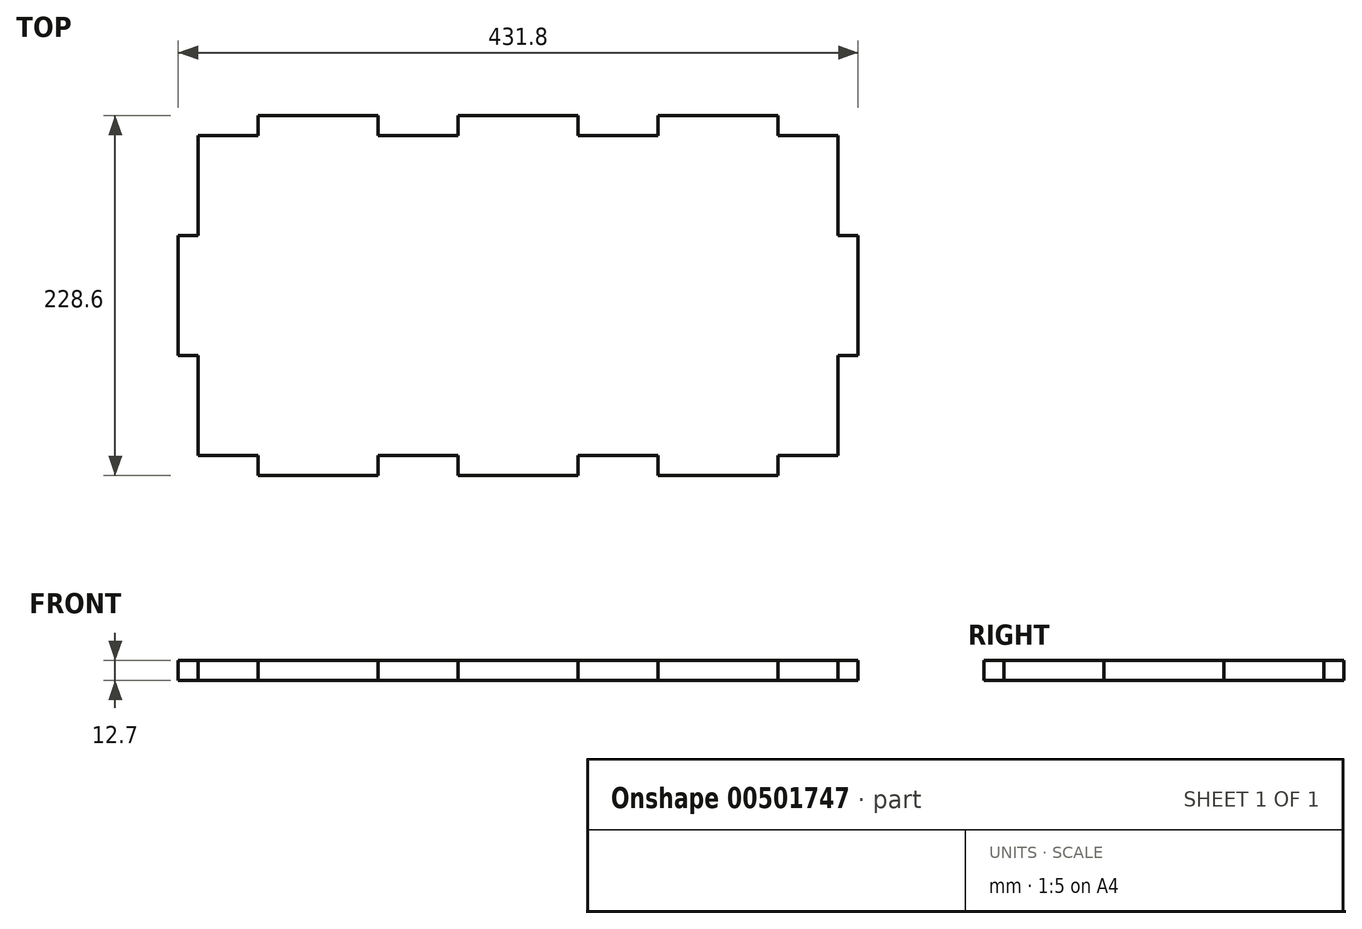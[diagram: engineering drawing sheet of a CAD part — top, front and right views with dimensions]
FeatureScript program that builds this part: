
annotation { "Feature Type Name" : "Feature", "Feature Type Description" : "" }
export const myFeature = defineFeature(function(context is Context, id is Id, definition is map)
    precondition{}
    {
        {
            var Q0;
            Q0=qCreatedBy(makeId("Top.planeOp"),FACE);
            var sketch = newSketch(context, id + "F0", { "sketchPlane" : qUnion([Q0])});
            skLineSegment(sketch, "E0.bottom", {"start": v(-203.2, 101.6) * mm, "end": v(203.2, 101.6) * mm});
            skLineSegment(sketch, "E0.top", {"start": v(-203.2, -101.6) * mm, "end": v(203.2, -101.6) * mm});
            skLineSegment(sketch, "E0.left", {"start": v(-203.2, 101.6) * mm, "end": v(-203.2, -101.6) * mm});
            skLineSegment(sketch, "E0.right", {"start": v(203.2, 101.6) * mm, "end": v(203.2, -101.6) * mm});
            skPoint(sketch, "E0.middle", {"position": v(0, 0) * mm});
            skLineSegment(sketch, "E1.bottom", {"start": v(-38.1, 114.3) * mm, "end": v(38.1, 114.3) * mm});
            skLineSegment(sketch, "E1.top", {"start": v(-38.1, 88.9) * mm, "end": v(38.1, 88.9) * mm});
            skLineSegment(sketch, "E1.left", {"start": v(-38.1, 114.3) * mm, "end": v(-38.1, 88.9) * mm});
            skLineSegment(sketch, "E1.right", {"start": v(38.1, 114.3) * mm, "end": v(38.1, 88.9) * mm});
            skPoint(sketch, "E1.middle", {"position": v(0, 101.6) * mm});
            skLineSegment(sketch, "E2.bottom", {"start": v(-215.9, 38.1) * mm, "end": v(-190.5, 38.1) * mm});
            skLineSegment(sketch, "E2.top", {"start": v(-215.9, -38.1) * mm, "end": v(-190.5, -38.1) * mm});
            skLineSegment(sketch, "E2.left", {"start": v(-215.9, 38.1) * mm, "end": v(-215.9, -38.1) * mm});
            skLineSegment(sketch, "E2.right", {"start": v(-190.5, 38.1) * mm, "end": v(-190.5, -38.1) * mm});
            skPoint(sketch, "E2.middle", {"position": v(-203.2, 0) * mm});
            skLineSegment(sketch, "E3.bottom", {"start": v(-38.1, -88.9) * mm, "end": v(38.1, -88.9) * mm});
            skLineSegment(sketch, "E3.top", {"start": v(-38.1, -114.3) * mm, "end": v(38.1, -114.3) * mm});
            skLineSegment(sketch, "E3.left", {"start": v(-38.1, -88.9) * mm, "end": v(-38.1, -114.3) * mm});
            skLineSegment(sketch, "E3.right", {"start": v(38.1, -88.9) * mm, "end": v(38.1, -114.3) * mm});
            skPoint(sketch, "E3.middle", {"position": v(0, -101.6) * mm});
            skLineSegment(sketch, "E4.bottom", {"start": v(190.5, 38.1) * mm, "end": v(215.9, 38.1) * mm});
            skLineSegment(sketch, "E4.top", {"start": v(190.5, -38.1) * mm, "end": v(215.9, -38.1) * mm});
            skLineSegment(sketch, "E4.left", {"start": v(190.5, 38.1) * mm, "end": v(190.5, -38.1) * mm});
            skLineSegment(sketch, "E4.right", {"start": v(215.9, 38.1) * mm, "end": v(215.9, -38.1) * mm});
            skPoint(sketch, "E4.middle", {"position": v(203.2, 0) * mm});
            skLineSegment(sketch, "E5.bottom", {"start": v(-165.1, -88.9) * mm, "end": v(-88.9, -88.9) * mm});
            skLineSegment(sketch, "E5.top", {"start": v(-165.1, -114.3) * mm, "end": v(-88.9, -114.3) * mm});
            skLineSegment(sketch, "E5.left", {"start": v(-165.1, -88.9) * mm, "end": v(-165.1, -114.3) * mm});
            skLineSegment(sketch, "E5.right", {"start": v(-88.9, -88.9) * mm, "end": v(-88.9, -114.3) * mm});
            skPoint(sketch, "E5.middle", {"position": v(-127, -101.6) * mm});
            skLineSegment(sketch, "E6.bottom", {"start": v(88.9, -88.9) * mm, "end": v(165.1, -88.9) * mm});
            skLineSegment(sketch, "E6.top", {"start": v(88.9, -114.3) * mm, "end": v(165.1, -114.3) * mm});
            skLineSegment(sketch, "E6.left", {"start": v(88.9, -88.9) * mm, "end": v(88.9, -114.3) * mm});
            skLineSegment(sketch, "E6.right", {"start": v(165.1, -88.9) * mm, "end": v(165.1, -114.3) * mm});
            skPoint(sketch, "E6.middle", {"position": v(127, -101.6) * mm});
            skLineSegment(sketch, "E7.bottom", {"start": v(-165.1, 88.9) * mm, "end": v(-88.9, 88.9) * mm});
            skLineSegment(sketch, "E7.top", {"start": v(-165.1, 114.3) * mm, "end": v(-88.9, 114.3) * mm});
            skLineSegment(sketch, "E7.left", {"start": v(-165.1, 88.9) * mm, "end": v(-165.1, 114.3) * mm});
            skLineSegment(sketch, "E7.right", {"start": v(-88.9, 88.9) * mm, "end": v(-88.9, 114.3) * mm});
            skPoint(sketch, "E7.middle", {"position": v(-127, 101.6) * mm});
            skPoint(sketch, "E7.middle.positionSnap0", {"position": v(-127, -88.9) * mm});
            skPoint(sketch, "E7.centerSnap0", {"position": v(-127, -88.9) * mm});
            skLineSegment(sketch, "E8.bottom", {"start": v(88.9, 114.3) * mm, "end": v(165.1, 114.3) * mm});
            skLineSegment(sketch, "E8.top", {"start": v(88.9, 88.9) * mm, "end": v(165.1, 88.9) * mm});
            skLineSegment(sketch, "E8.left", {"start": v(88.9, 114.3) * mm, "end": v(88.9, 88.9) * mm});
            skLineSegment(sketch, "E8.right", {"start": v(165.1, 114.3) * mm, "end": v(165.1, 88.9) * mm});
            skPoint(sketch, "E8.middle", {"position": v(127, 101.6) * mm});
            skPoint(sketch, "E8.middle.positionSnap0", {"position": v(127, -88.9) * mm});
            skPoint(sketch, "E8.centerSnap0", {"position": v(127, -88.9) * mm});
            skSolve(sketch);
        }
        {
            var Q0;
            {var subQ1=sQuery(id+"F0.wireOp",EDGE,"E1.top");Q0=makeQuery(id+"F0.imprint","IMPRINT",FACE,{"disambiguationData":[TD([[makeQuery(id+"F0.imprint","IMPRINT",EDGE,{"derivedFrom":subQ1}),-1.0]])]});}
            var Q1;
            {var subQ5=sQuery(id+"F0.wireOp",EDGE,"E2.right");Q1=makeQuery(id+"F0.imprint","IMPRINT",FACE,{"disambiguationData":[TD([[makeQuery(id+"F0.imprint","IMPRINT",EDGE,{"derivedFrom":subQ5}),-1.0]])]});}
            var Q2;
            {var subQ5=sQuery(id+"F0.wireOp",EDGE,"E2.left");Q2=makeQuery(id+"F0.imprint","IMPRINT",FACE,{"disambiguationData":[TD([[makeQuery(id+"F0.imprint","IMPRINT",EDGE,{"derivedFrom":subQ5}),1.0]])]});}
            var Q3;
            {var subQ5=sQuery(id+"F0.wireOp",EDGE,"E1.bottom");Q3=makeQuery(id+"F0.imprint","IMPRINT",FACE,{"disambiguationData":[TD([[makeQuery(id+"F0.imprint","IMPRINT",EDGE,{"derivedFrom":subQ5}),-1.0]])]});}
            var Q4;
            {var subQ5=sQuery(id+"F0.wireOp",EDGE,"E1.top");Q4=makeQuery(id+"F0.imprint","IMPRINT",FACE,{"disambiguationData":[TD([[makeQuery(id+"F0.imprint","IMPRINT",EDGE,{"derivedFrom":subQ5}),1.0]])]});}
            var Q5;
            {var subQ5=sQuery(id+"F0.wireOp",EDGE,"E3.top");Q5=makeQuery(id+"F0.imprint","IMPRINT",FACE,{"disambiguationData":[TD([[makeQuery(id+"F0.imprint","IMPRINT",EDGE,{"derivedFrom":subQ5}),1.0]])]});}
            var Q6;
            {var subQ5=sQuery(id+"F0.wireOp",EDGE,"E3.bottom");Q6=makeQuery(id+"F0.imprint","IMPRINT",FACE,{"disambiguationData":[TD([[makeQuery(id+"F0.imprint","IMPRINT",EDGE,{"derivedFrom":subQ5}),-1.0]])]});}
            var Q7;
            {var subQ5=sQuery(id+"F0.wireOp",EDGE,"E4.left");Q7=makeQuery(id+"F0.imprint","IMPRINT",FACE,{"disambiguationData":[TD([[makeQuery(id+"F0.imprint","IMPRINT",EDGE,{"derivedFrom":subQ5}),1.0]])]});}
            var Q8;
            {var subQ5=sQuery(id+"F0.wireOp",EDGE,"E4.right");Q8=makeQuery(id+"F0.imprint","IMPRINT",FACE,{"disambiguationData":[TD([[makeQuery(id+"F0.imprint","IMPRINT",EDGE,{"derivedFrom":subQ5}),-1.0]])]});}
            var Q9;
            {var subQ5=sQuery(id+"F0.wireOp",EDGE,"E7.top");Q9=makeQuery(id+"F0.imprint","IMPRINT",FACE,{"disambiguationData":[TD([[makeQuery(id+"F0.imprint","IMPRINT",EDGE,{"derivedFrom":subQ5}),-1.0]])]});}
            var Q10;
            {var subQ5=sQuery(id+"F0.wireOp",EDGE,"E7.bottom");Q10=makeQuery(id+"F0.imprint","IMPRINT",FACE,{"disambiguationData":[TD([[makeQuery(id+"F0.imprint","IMPRINT",EDGE,{"derivedFrom":subQ5}),1.0]])]});}
            var Q11;
            {var subQ5=sQuery(id+"F0.wireOp",EDGE,"E8.top");Q11=makeQuery(id+"F0.imprint","IMPRINT",FACE,{"disambiguationData":[TD([[makeQuery(id+"F0.imprint","IMPRINT",EDGE,{"derivedFrom":subQ5}),1.0]])]});}
            var Q12;
            {var subQ5=sQuery(id+"F0.wireOp",EDGE,"E8.bottom");Q12=makeQuery(id+"F0.imprint","IMPRINT",FACE,{"disambiguationData":[TD([[makeQuery(id+"F0.imprint","IMPRINT",EDGE,{"derivedFrom":subQ5}),-1.0]])]});}
            var Q13;
            {var subQ5=sQuery(id+"F0.wireOp",EDGE,"E6.bottom");Q13=makeQuery(id+"F0.imprint","IMPRINT",FACE,{"disambiguationData":[TD([[makeQuery(id+"F0.imprint","IMPRINT",EDGE,{"derivedFrom":subQ5}),-1.0]])]});}
            var Q14;
            {var subQ5=sQuery(id+"F0.wireOp",EDGE,"E6.top");Q14=makeQuery(id+"F0.imprint","IMPRINT",FACE,{"disambiguationData":[TD([[makeQuery(id+"F0.imprint","IMPRINT",EDGE,{"derivedFrom":subQ5}),1.0]])]});}
            var Q15;
            {var subQ5=sQuery(id+"F0.wireOp",EDGE,"E5.bottom");Q15=makeQuery(id+"F0.imprint","IMPRINT",FACE,{"disambiguationData":[TD([[makeQuery(id+"F0.imprint","IMPRINT",EDGE,{"derivedFrom":subQ5}),-1.0]])]});}
            var Q16;
            {var subQ5=sQuery(id+"F0.wireOp",EDGE,"E5.top");Q16=makeQuery(id+"F0.imprint","IMPRINT",FACE,{"disambiguationData":[TD([[makeQuery(id+"F0.imprint","IMPRINT",EDGE,{"derivedFrom":subQ5}),1.0]])]});}
            extrude(context, id + "F1", {"entities" : qUnion([Q0, Q1, Q2, Q3, Q4, Q5, Q6, Q7, Q8, Q9, Q10, Q11, Q12, Q13, Q14, Q15, Q16]), "depth" : 12.7 * mm, "offsetDistance" : 25.4 * mm});
        }
    });
